# Revit family: Lodestar 12' x 12' Base - Sharable - 11-24
name_source: partatom
category: Generic Models
units: mm (PartAtom-declared; Revit-internal decimal feet)

## family parameters
Always vertical = Yes
Can host rebar = No
Cut with Voids When Loaded = No
Maintain Annotation Orientation = No
Part Type = Normal
Room Calculation Point = No
Round Connector Dimension = Use Diameter
Shared = No
Work Plane-Based = No

## types (1)
- MBB144 - 3658x3658
    Base visibility Y/N = Yes
    Default Elevation = -750 mm  [stored -2.46063 ft]
    Fastener Material = <By Category>
    Material Concrete = Concrete, Precast
    Material Slab = Concrete, Precast
    Material Steel = Steel
    Material Subbase Fill = Earth - Gravel
    Steel Material = <By Category>
    Structural Fasteners = Yes
    base_baseHeight = 600 mm
    base_lowerTierHeight = 225 mm  [stored 0.738189 ft]
    base_mainChamfer = 19 mm  [stored 0.062336 ft]
    base_perimeterBeamSpacing = 1500 mm
    base_perimeterThickness = 327 mm
    base_totalHeight = 600 mm
    base_totalLength = 9000 mm
    base_totalWidth = 4500 mm
    base_transverseBeamThickness = 160 mm
    base_tranverseBeamSpan = 3211 mm  [stored 10.5348 ft]
    base_upperTierHeight = 375 mm  [stored 1.23031 ft]
    base_widthLowerTier = 317 mm
    constraint_columnPosition = 175 mm
    logic_type144 = No
    logic_type218 = No
    logic_type288 = No
    logic_type436 = Yes
    slab_castInPlaceSlabThickness = 150 mm
    steelFooting_connectionHeight = 125 mm
    steelFooting_plateSquare = 270 mm
    steelFooting_plateThickness = 13 mm
    utilityPort_radiusLarge = 56 mm  [stored 0.183727 ft]
    utilityPort_radiusSmall = 28 mm  [stored 0.0918635 ft]

note: [stored X ft] marks values corroborated as IEEE doubles in the binary element streams (Revit-internal decimal feet)

## geometry (parser evidence)
native form markers: Sweep x2
no freeform markers — native parametric forms only
